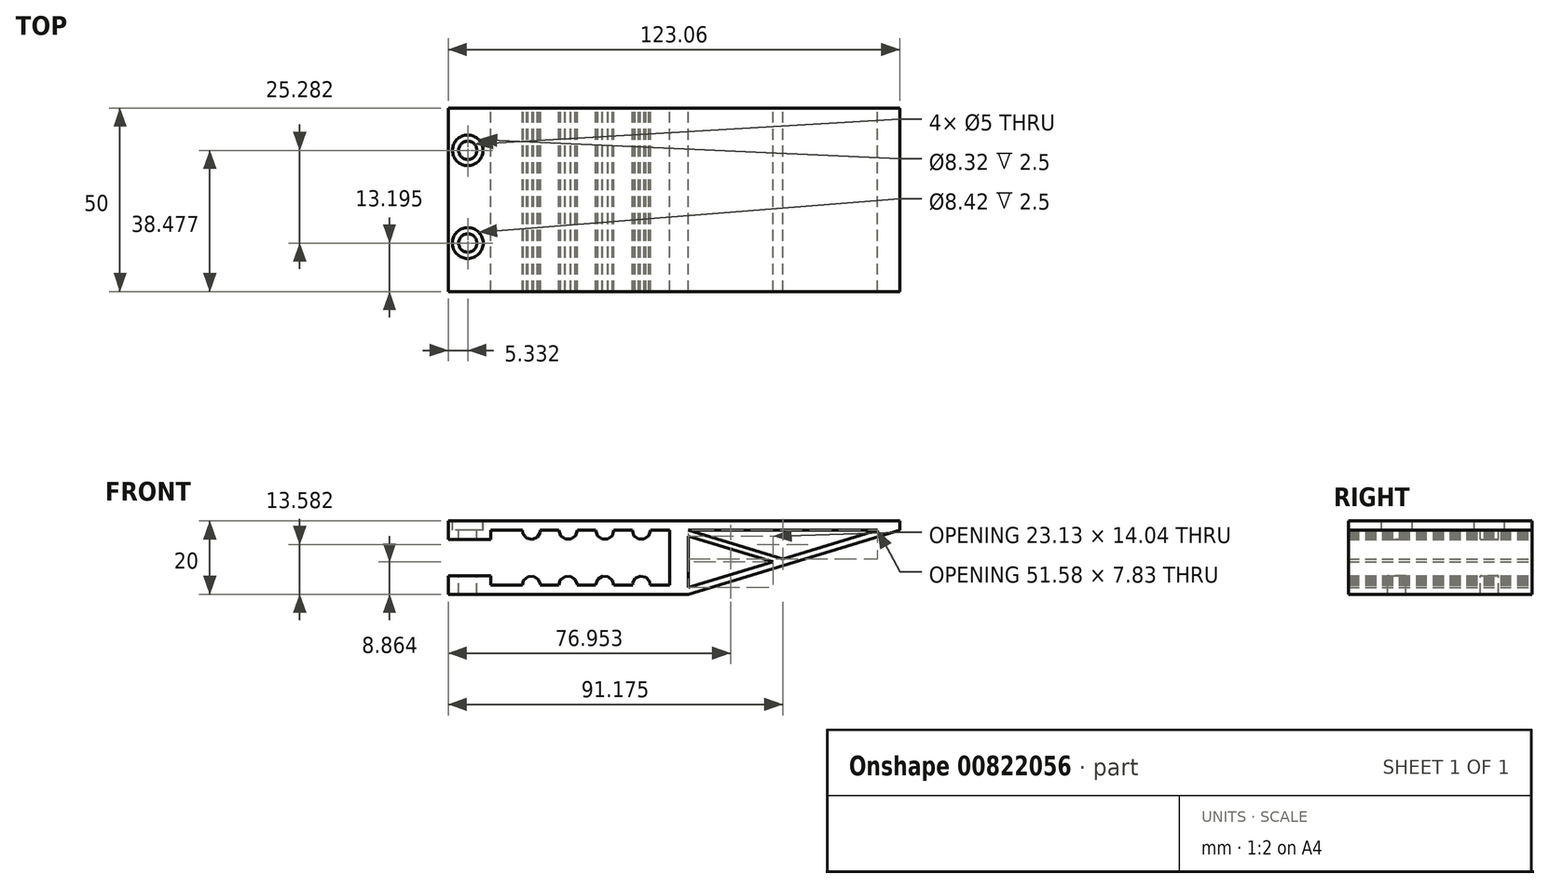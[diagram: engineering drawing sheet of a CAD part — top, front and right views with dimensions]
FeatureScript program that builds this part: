
annotation { "Feature Type Name" : "Feature", "Feature Type Description" : "" }
export const myFeature = defineFeature(function(context is Context, id is Id, definition is map)
    precondition{}
    {
        {
            var Q0;
            Q0=qCreatedBy(makeId("Front.planeOp"),FACE);
            var sketch = newSketch(context, id + "F0", { "sketchPlane" : qUnion([Q0])});
            skLineSegment(sketch, "E0.bottom", {"start": v(-74.58, 29.93) * mm, "end": v(-63, 29.93) * mm});
            skLineSegment(sketch, "E0.top", {"start": v(-74.58, 24.93) * mm, "end": v(-63, 24.93) * mm});
            skLineSegment(sketch, "E0.left", {"start": v(-74.58, 29.93) * mm, "end": v(-74.58, 24.93) * mm});
            skLineSegment(sketch, "E0.right", {"start": v(-63, 29.93) * mm, "end": v(-63, 24.93) * mm});
            skLineSegment(sketch, "E1.bottom", {"start": v(-74.58, 14.93) * mm, "end": v(-63, 14.93) * mm});
            skLineSegment(sketch, "E1.top", {"start": v(-74.58, 9.93) * mm, "end": v(-63, 9.93) * mm});
            skLineSegment(sketch, "E1.left", {"start": v(-74.58, 14.93) * mm, "end": v(-74.58, 9.93) * mm});
            skLineSegment(sketch, "E1.right", {"start": v(-63, 14.93) * mm, "end": v(-63, 9.93) * mm});
            skPoint(sketch, "E2.oppositeSnap0", {"position": v(-63, 27.43) * mm});
            skLineSegment(sketch, "E2.bottom", {"start": v(-63, 29.93) * mm, "end": v(-14.2, 29.93) * mm});
            skLineSegment(sketch, "E2.top", {"start": v(-63, 27.43) * mm, "end": v(-14.2, 27.43) * mm});
            skLineSegment(sketch, "E2.left", {"start": v(-63, 29.93) * mm, "end": v(-63, 27.43) * mm});
            skLineSegment(sketch, "E2.right", {"start": v(-14.2, 29.93) * mm, "end": v(-14.2, 27.43) * mm});
            skLineSegment(sketch, "E3.bottom", {"start": v(-63, 9.93) * mm, "end": v(-14.2, 9.93) * mm});
            skLineSegment(sketch, "E3.top", {"start": v(-63, 12.43) * mm, "end": v(-14.2, 12.43) * mm});
            skLineSegment(sketch, "E3.left", {"start": v(-63, 9.93) * mm, "end": v(-63, 12.43) * mm});
            skLineSegment(sketch, "E3.right", {"start": v(-14.2, 9.93) * mm, "end": v(-14.2, 12.43) * mm});
            skLineSegment(sketch, "E4.bottom", {"start": v(-14.2, 29.93) * mm, "end": v(-9.2, 29.93) * mm});
            skLineSegment(sketch, "E4.top", {"start": v(-14.2, 9.93) * mm, "end": v(-9.2, 9.93) * mm});
            skLineSegment(sketch, "E4.left", {"start": v(-14.2, 29.93) * mm, "end": v(-14.2, 9.93) * mm});
            skLineSegment(sketch, "E4.right", {"start": v(-9.2, 29.93) * mm, "end": v(-9.2, 9.93) * mm});
            skCircle(sketch, "E5.cCircle", {"center": v(-51.92, 27.43) * mm, "radius": 2.5 * mm, "construction": true});
            skLineSegment(sketch, "E5.0", {"start": v(-53.23, 25.3) * mm, "end": v(-54.23, 26.47) * mm});
            skLineSegment(sketch, "E5.1", {"start": v(-54.23, 26.47) * mm, "end": v(-54.35, 28.01) * mm});
            skLineSegment(sketch, "E5.2", {"start": v(-54.35, 28.01) * mm, "end": v(-53.54, 29.33) * mm});
            skLineSegment(sketch, "E5.3", {"start": v(-53.54, 29.33) * mm, "end": v(-52.11, 29.92) * mm});
            skLineSegment(sketch, "E5.4", {"start": v(-52.11, 29.92) * mm, "end": v(-50.61, 29.55) * mm});
            skLineSegment(sketch, "E5.5", {"start": v(-50.61, 29.55) * mm, "end": v(-49.6, 28.38) * mm});
            skLineSegment(sketch, "E5.6", {"start": v(-49.6, 28.38) * mm, "end": v(-49.5, 26.84) * mm});
            skLineSegment(sketch, "E5.7", {"start": v(-49.5, 26.84) * mm, "end": v(-50.3, 25.52) * mm});
            skLineSegment(sketch, "E5.8", {"start": v(-50.3, 25.52) * mm, "end": v(-51.73, 24.93) * mm});
            skLineSegment(sketch, "E5.9", {"start": v(-51.73, 24.93) * mm, "end": v(-53.23, 25.3) * mm});
            skCircle(sketch, "E6.cCircle", {"center": v(-41.92, 27.43) * mm, "radius": 2.5 * mm, "construction": true});
            skLineSegment(sketch, "E6.0", {"start": v(-44.42, 27.43) * mm, "end": v(-43.94, 28.9) * mm});
            skLineSegment(sketch, "E6.1", {"start": v(-43.94, 28.9) * mm, "end": v(-42.7, 29.8) * mm});
            skLineSegment(sketch, "E6.2", {"start": v(-42.7, 29.8) * mm, "end": v(-41.15, 29.8) * mm});
            skLineSegment(sketch, "E6.3", {"start": v(-41.15, 29.8) * mm, "end": v(-39.9, 28.9) * mm});
            skLineSegment(sketch, "E6.4", {"start": v(-39.9, 28.9) * mm, "end": v(-39.42, 27.43) * mm});
            skLineSegment(sketch, "E6.5", {"start": v(-39.42, 27.43) * mm, "end": v(-39.9, 25.96) * mm});
            skLineSegment(sketch, "E6.6", {"start": v(-39.9, 25.96) * mm, "end": v(-41.15, 25.05) * mm});
            skLineSegment(sketch, "E6.7", {"start": v(-41.15, 25.05) * mm, "end": v(-42.7, 25.05) * mm});
            skLineSegment(sketch, "E6.8", {"start": v(-42.7, 25.05) * mm, "end": v(-43.94, 25.96) * mm});
            skLineSegment(sketch, "E6.9", {"start": v(-43.94, 25.96) * mm, "end": v(-44.42, 27.43) * mm});
            skCircle(sketch, "E7.cCircle", {"center": v(-31.92, 27.43) * mm, "radius": 2.5 * mm, "construction": true});
            skLineSegment(sketch, "E7.0", {"start": v(-34.42, 27.43) * mm, "end": v(-33.94, 28.9) * mm});
            skLineSegment(sketch, "E7.1", {"start": v(-33.94, 28.9) * mm, "end": v(-32.7, 29.8) * mm});
            skLineSegment(sketch, "E7.2", {"start": v(-32.7, 29.8) * mm, "end": v(-31.15, 29.8) * mm});
            skLineSegment(sketch, "E7.3", {"start": v(-31.15, 29.8) * mm, "end": v(-29.9, 28.9) * mm});
            skLineSegment(sketch, "E7.4", {"start": v(-29.9, 28.9) * mm, "end": v(-29.42, 27.43) * mm});
            skLineSegment(sketch, "E7.5", {"start": v(-29.42, 27.43) * mm, "end": v(-29.9, 25.96) * mm});
            skLineSegment(sketch, "E7.6", {"start": v(-29.9, 25.96) * mm, "end": v(-31.15, 25.05) * mm});
            skLineSegment(sketch, "E7.7", {"start": v(-31.15, 25.05) * mm, "end": v(-32.7, 25.05) * mm});
            skLineSegment(sketch, "E7.8", {"start": v(-32.7, 25.05) * mm, "end": v(-33.94, 25.96) * mm});
            skLineSegment(sketch, "E7.9", {"start": v(-33.94, 25.96) * mm, "end": v(-34.42, 27.43) * mm});
            skCircle(sketch, "E8.cCircle", {"center": v(-21.92, 27.43) * mm, "radius": 2.5 * mm, "construction": true});
            skLineSegment(sketch, "E8.0", {"start": v(-24.42, 27.43) * mm, "end": v(-23.94, 28.9) * mm});
            skLineSegment(sketch, "E8.1", {"start": v(-23.94, 28.9) * mm, "end": v(-22.7, 29.8) * mm});
            skLineSegment(sketch, "E8.2", {"start": v(-22.7, 29.8) * mm, "end": v(-21.15, 29.8) * mm});
            skLineSegment(sketch, "E8.3", {"start": v(-21.15, 29.8) * mm, "end": v(-19.9, 28.9) * mm});
            skLineSegment(sketch, "E8.4", {"start": v(-19.9, 28.9) * mm, "end": v(-19.42, 27.43) * mm});
            skLineSegment(sketch, "E8.5", {"start": v(-19.42, 27.43) * mm, "end": v(-19.9, 25.96) * mm});
            skLineSegment(sketch, "E8.6", {"start": v(-19.9, 25.96) * mm, "end": v(-21.15, 25.05) * mm});
            skLineSegment(sketch, "E8.7", {"start": v(-21.15, 25.05) * mm, "end": v(-22.7, 25.05) * mm});
            skLineSegment(sketch, "E8.8", {"start": v(-22.7, 25.05) * mm, "end": v(-23.94, 25.96) * mm});
            skLineSegment(sketch, "E8.9", {"start": v(-23.94, 25.96) * mm, "end": v(-24.42, 27.43) * mm});
            skCircle(sketch, "E9.cCircle", {"center": v(-51.92, 12.43) * mm, "radius": 2.5 * mm, "construction": true});
            skLineSegment(sketch, "E9.0", {"start": v(-51.3, 14.85) * mm, "end": v(-50, 14.03) * mm});
            skLineSegment(sketch, "E9.1", {"start": v(-50, 14.03) * mm, "end": v(-49.43, 12.6) * mm});
            skLineSegment(sketch, "E9.2", {"start": v(-49.43, 12.6) * mm, "end": v(-49.8, 11.1) * mm});
            skLineSegment(sketch, "E9.3", {"start": v(-49.8, 11.1) * mm, "end": v(-51, 10.1) * mm});
            skLineSegment(sketch, "E9.4", {"start": v(-51, 10.1) * mm, "end": v(-52.53, 10) * mm});
            skLineSegment(sketch, "E9.5", {"start": v(-52.53, 10) * mm, "end": v(-53.84, 10.82) * mm});
            skLineSegment(sketch, "E9.6", {"start": v(-53.84, 10.82) * mm, "end": v(-54.42, 12.26) * mm});
            skLineSegment(sketch, "E9.7", {"start": v(-54.42, 12.26) * mm, "end": v(-54.04, 13.76) * mm});
            skLineSegment(sketch, "E9.8", {"start": v(-54.04, 13.76) * mm, "end": v(-52.85, 14.75) * mm});
            skLineSegment(sketch, "E9.9", {"start": v(-52.85, 14.75) * mm, "end": v(-51.3, 14.85) * mm});
            skCircle(sketch, "E10.cCircle", {"center": v(-41.92, 12.43) * mm, "radius": 2.5 * mm, "construction": true});
            skLineSegment(sketch, "E10.0", {"start": v(-41.27, 14.84) * mm, "end": v(-39.98, 14) * mm});
            skLineSegment(sketch, "E10.1", {"start": v(-39.98, 14) * mm, "end": v(-39.42, 12.55) * mm});
            skLineSegment(sketch, "E10.2", {"start": v(-39.42, 12.55) * mm, "end": v(-39.83, 11.06) * mm});
            skLineSegment(sketch, "E10.3", {"start": v(-39.83, 11.06) * mm, "end": v(-41.03, 10.09) * mm});
            skLineSegment(sketch, "E10.4", {"start": v(-41.03, 10.09) * mm, "end": v(-42.57, 10.01) * mm});
            skLineSegment(sketch, "E10.5", {"start": v(-42.57, 10.01) * mm, "end": v(-43.87, 10.86) * mm});
            skLineSegment(sketch, "E10.6", {"start": v(-43.87, 10.86) * mm, "end": v(-44.42, 12.3) * mm});
            skLineSegment(sketch, "E10.7", {"start": v(-44.42, 12.3) * mm, "end": v(-44.02, 13.8) * mm});
            skLineSegment(sketch, "E10.8", {"start": v(-44.02, 13.8) * mm, "end": v(-42.81, 14.76) * mm});
            skLineSegment(sketch, "E10.9", {"start": v(-42.81, 14.76) * mm, "end": v(-41.27, 14.84) * mm});
            skCircle(sketch, "E11.cCircle", {"center": v(-31.92, 12.43) * mm, "radius": 2.5 * mm, "construction": true});
            skLineSegment(sketch, "E11.0", {"start": v(-30.98, 14.74) * mm, "end": v(-29.8, 13.75) * mm});
            skLineSegment(sketch, "E11.1", {"start": v(-29.8, 13.75) * mm, "end": v(-29.43, 12.25) * mm});
            skLineSegment(sketch, "E11.2", {"start": v(-29.43, 12.25) * mm, "end": v(-30, 10.82) * mm});
            skLineSegment(sketch, "E11.3", {"start": v(-30, 10.82) * mm, "end": v(-31.32, 10) * mm});
            skLineSegment(sketch, "E11.4", {"start": v(-31.32, 10) * mm, "end": v(-32.86, 10.1) * mm});
            skLineSegment(sketch, "E11.5", {"start": v(-32.86, 10.1) * mm, "end": v(-34.04, 11.1) * mm});
            skLineSegment(sketch, "E11.6", {"start": v(-34.04, 11.1) * mm, "end": v(-34.41, 12.6) * mm});
            skLineSegment(sketch, "E11.7", {"start": v(-34.41, 12.6) * mm, "end": v(-33.84, 14.03) * mm});
            skLineSegment(sketch, "E11.8", {"start": v(-33.84, 14.03) * mm, "end": v(-32.52, 14.85) * mm});
            skLineSegment(sketch, "E11.9", {"start": v(-32.52, 14.85) * mm, "end": v(-30.98, 14.74) * mm});
            skCircle(sketch, "E12.cCircle", {"center": v(-21.92, 12.43) * mm, "radius": 2.5 * mm, "construction": true});
            skLineSegment(sketch, "E12.0", {"start": v(-22.18, 14.91) * mm, "end": v(-20.67, 14.59) * mm});
            skLineSegment(sketch, "E12.1", {"start": v(-20.67, 14.59) * mm, "end": v(-19.64, 13.44) * mm});
            skLineSegment(sketch, "E12.2", {"start": v(-19.64, 13.44) * mm, "end": v(-19.48, 11.9) * mm});
            skLineSegment(sketch, "E12.3", {"start": v(-19.48, 11.9) * mm, "end": v(-20.25, 10.57) * mm});
            skLineSegment(sketch, "E12.4", {"start": v(-20.25, 10.57) * mm, "end": v(-21.66, 9.94) * mm});
            skLineSegment(sketch, "E12.5", {"start": v(-21.66, 9.94) * mm, "end": v(-23.17, 10.26) * mm});
            skLineSegment(sketch, "E12.6", {"start": v(-23.17, 10.26) * mm, "end": v(-24.2, 11.41) * mm});
            skLineSegment(sketch, "E12.7", {"start": v(-24.2, 11.41) * mm, "end": v(-24.37, 12.95) * mm});
            skLineSegment(sketch, "E12.8", {"start": v(-24.37, 12.95) * mm, "end": v(-23.6, 14.29) * mm});
            skLineSegment(sketch, "E12.9", {"start": v(-23.6, 14.29) * mm, "end": v(-22.18, 14.91) * mm});
            skLineSegment(sketch, "E13.bottom", {"start": v(-9.2, 27.43) * mm, "end": v(48.48, 27.43) * mm});
            skLineSegment(sketch, "E13.top", {"start": v(-9.2, 29.93) * mm, "end": v(48.48, 29.93) * mm});
            skLineSegment(sketch, "E13.left", {"start": v(-9.2, 27.43) * mm, "end": v(-9.2, 29.93) * mm});
            skLineSegment(sketch, "E13.right", {"start": v(48.48, 27.43) * mm, "end": v(48.48, 29.93) * mm});
            skLineSegment(sketch, "E14", {"start": v(-9.2, 9.93) * mm, "end": v(48.48, 27.43) * mm});
            skLineSegment(sketch, "E15", {"start": v(42.38, 27.43) * mm, "end": v(-9.2, 11.77) * mm});
            skLineSegment(sketch, "E16", {"start": v(-9.2, 27.43) * mm, "end": v(16.6, 19.6) * mm});
            skLineSegment(sketch, "E17", {"start": v(13.94, 18.8) * mm, "end": v(-9.2, 25.81) * mm});
            skSolve(sketch);
        }
        {
            var Q0;
            Q0=makeQuery(id+"F0.imprint","IMPRINT",FACE,{"disambiguationData":[TD([[makeQuery(id+"F0.imprint","IMPRINT",EDGE,{"derivedFrom":sQuery(id+"F0.wireOp",EDGE,"E1.bottom")}),-1.0]])]});
            var Q1;
            Q1=makeQuery(id+"F0.imprint","IMPRINT",FACE,{"disambiguationData":[TD([[makeQuery(id+"F0.imprint","IMPRINT",EDGE,{"derivedFrom":sQuery(id+"F0.wireOp",EDGE,"E0.bottom")}),-1.0]])]});
            var Q2;
            {var subQ5=sQuery(id+"F0.wireOp",EDGE,"E5.0");Q2=makeQuery(id+"F0.imprint","IMPRINT",FACE,{"disambiguationData":[TD([[makeQuery(id+"F0.imprint","IMPRINT",EDGE,{"derivedFrom":subQ5}),-1.0]])]});}
            var Q3;
            {var subQ9=sQuery(id+"F0.wireOp",EDGE,"E2.bottom");Q3=makeQuery(id+"F0.imprint","IMPRINT",FACE,{"disambiguationData":[TD([[makeQuery(id+"F0.imprint","IMPRINT",EDGE,{"derivedFrom":subQ9}),-1.0]])]});}
            var Q4;
            {var subQ0=sQuery(id+"F0.wireOp",EDGE,"E5.2");Q4=makeQuery(id+"F0.imprint","IMPRINT",FACE,{"disambiguationData":[TD([[makeQuery(id+"F0.imprint","IMPRINT",EDGE,{"derivedFrom":subQ0}),-1.0]])]});}
            var Q5;
            {var subQ0=sQuery(id+"F0.wireOp",EDGE,"E6.0");Q5=makeQuery(id+"F0.imprint","IMPRINT",FACE,{"disambiguationData":[TD([[makeQuery(id+"F0.imprint","IMPRINT",EDGE,{"derivedFrom":subQ0}),-1.0]])]});}
            var Q6;
            {var subQ2=sQuery(id+"F0.wireOp",EDGE,"E6.5");Q6=makeQuery(id+"F0.imprint","IMPRINT",FACE,{"disambiguationData":[TD([[makeQuery(id+"F0.imprint","IMPRINT",EDGE,{"derivedFrom":subQ2}),-1.0]])]});}
            var Q7;
            {var subQ0=sQuery(id+"F0.wireOp",EDGE,"E7.5");Q7=makeQuery(id+"F0.imprint","IMPRINT",FACE,{"disambiguationData":[TD([[makeQuery(id+"F0.imprint","IMPRINT",EDGE,{"derivedFrom":subQ0}),-1.0]])]});}
            var Q8;
            {var subQ0=sQuery(id+"F0.wireOp",EDGE,"E7.0");Q8=makeQuery(id+"F0.imprint","IMPRINT",FACE,{"disambiguationData":[TD([[makeQuery(id+"F0.imprint","IMPRINT",EDGE,{"derivedFrom":subQ0}),-1.0]])]});}
            var Q9;
            {var subQ0=sQuery(id+"F0.wireOp",EDGE,"E8.0");Q9=makeQuery(id+"F0.imprint","IMPRINT",FACE,{"disambiguationData":[TD([[makeQuery(id+"F0.imprint","IMPRINT",EDGE,{"derivedFrom":subQ0}),-1.0]])]});}
            var Q10;
            {var subQ0=sQuery(id+"F0.wireOp",EDGE,"E8.5");Q10=makeQuery(id+"F0.imprint","IMPRINT",FACE,{"disambiguationData":[TD([[makeQuery(id+"F0.imprint","IMPRINT",EDGE,{"derivedFrom":subQ0}),-1.0]])]});}
            var Q11;
            Q11=makeQuery(id+"F0.imprint","IMPRINT",FACE,{"disambiguationData":[TD([[makeQuery(id+"F0.imprint","IMPRINT",EDGE,{"derivedFrom":sQuery(id+"F0.wireOp",EDGE,"E9.0")}),-1.0]])]});
            var Q12;
            {var subQ0=sQuery(id+"F0.wireOp",EDGE,"E9.3");Q12=makeQuery(id+"F0.imprint","IMPRINT",FACE,{"disambiguationData":[TD([[makeQuery(id+"F0.imprint","IMPRINT",EDGE,{"derivedFrom":subQ0}),-1.0]])]});}
            var Q13;
            Q13=makeQuery(id+"F0.imprint","IMPRINT",FACE,{"disambiguationData":[TD([[makeQuery(id+"F0.imprint","IMPRINT",EDGE,{"derivedFrom":sQuery(id+"F0.wireOp",EDGE,"E10.0")}),-1.0]])]});
            var Q14;
            {var subQ0=sQuery(id+"F0.wireOp",EDGE,"E10.3");Q14=makeQuery(id+"F0.imprint","IMPRINT",FACE,{"disambiguationData":[TD([[makeQuery(id+"F0.imprint","IMPRINT",EDGE,{"derivedFrom":subQ0}),-1.0]])]});}
            var Q15;
            {var subQ4=sQuery(id+"F0.wireOp",EDGE,"E11.0");Q15=makeQuery(id+"F0.imprint","IMPRINT",FACE,{"disambiguationData":[TD([[makeQuery(id+"F0.imprint","IMPRINT",EDGE,{"derivedFrom":subQ4}),-1.0]])]});}
            var Q16;
            {var subQ0=sQuery(id+"F0.wireOp",EDGE,"E11.2");Q16=makeQuery(id+"F0.imprint","IMPRINT",FACE,{"disambiguationData":[TD([[makeQuery(id+"F0.imprint","IMPRINT",EDGE,{"derivedFrom":subQ0}),-1.0]])]});}
            var Q17;
            Q17=makeQuery(id+"F0.imprint","IMPRINT",FACE,{"disambiguationData":[TD([[makeQuery(id+"F0.imprint","IMPRINT",EDGE,{"derivedFrom":sQuery(id+"F0.wireOp",EDGE,"E12.0")}),-1.0]])]});
            var Q18;
            {var subQ0=sQuery(id+"F0.wireOp",EDGE,"E12.3");Q18=makeQuery(id+"F0.imprint","IMPRINT",FACE,{"disambiguationData":[TD([[makeQuery(id+"F0.imprint","IMPRINT",EDGE,{"derivedFrom":subQ0}),-1.0]])]});}
            var Q19;
            {var subQ15=sQuery(id+"F0.wireOp",EDGE,"E3.bottom");Q19=makeQuery(id+"F0.imprint","IMPRINT",FACE,{"disambiguationData":[TD([[makeQuery(id+"F0.imprint","IMPRINT",EDGE,{"derivedFrom":subQ15}),1.0]])]});}
            var Q20;
            {var subQ3=sQuery(id+"F0.wireOp",EDGE,"E4.bottom");Q20=makeQuery(id+"F0.imprint","IMPRINT",FACE,{"disambiguationData":[TD([[makeQuery(id+"F0.imprint","IMPRINT",EDGE,{"derivedFrom":subQ3}),-1.0]])]});}
            var Q21;
            Q21=makeQuery(id+"F0.imprint","IMPRINT",FACE,{"disambiguationData":[TD([[makeQuery(id+"F0.imprint","IMPRINT",EDGE,{"derivedFrom":sQuery(id+"F0.wireOp",EDGE,"E13.top")}),-1.0]])]});
            var Q22;
            {var subQ0=sQuery(id+"F0.wireOp",EDGE,"E16");Q22=makeQuery(id+"F0.imprint","IMPRINT",FACE,{"disambiguationData":[TD([[makeQuery(id+"F0.imprint","IMPRINT",EDGE,{"derivedFrom":subQ0}),-1.0]])]});}
            var Q23;
            {var subQ0=sQuery(id+"F0.wireOp",EDGE,"E14");Q23=makeQuery(id+"F0.imprint","IMPRINT",FACE,{"disambiguationData":[TD([[makeQuery(id+"F0.imprint","IMPRINT",EDGE,{"derivedFrom":subQ0}),1.0]])]});}
            extrude(context, id + "F1", {"entities" : qUnion([Q0, Q1, Q2, Q3, Q4, Q5, Q6, Q7, Q8, Q9, Q10, Q11, Q12, Q13, Q14, Q15, Q16, Q17, Q18, Q19, Q20, Q21, Q22, Q23]), "depth" : 50 * mm, "offsetDistance" : 25 * mm});
        }
        {
            var Q0;
            Q0=makeQuery(id+"F1.opExtrude","SWEPT_FACE",FACE,{"disambiguationData":[OSD([sQuery(id+"F0.wireOp",EDGE,"E0.bottom"),sQuery(id+"F0.wireOp",EDGE,"E2.bottom"),sQuery(id+"F0.wireOp",EDGE,"E4.bottom"),sQuery(id+"F0.wireOp",EDGE,"E13.top")])]});
            var sketch = newSketch(context, id + "F2", { "sketchPlane" : qUnion([Q0])});
            skPoint(sketch, "E18", {"position": v(-69.25, -11.52) * mm});
            skPoint(sketch, "E19", {"position": v(-69.25, -36.8) * mm});
            skSolve(sketch);
        }
        {
            var Q0;
            Q0=sQuery(id+"F2.wireOp",VERTEX,"E18");
            var Q1;
            Q1=sQuery(id+"F2.wireOp",VERTEX,"E19");
            var Q2;
            Q2=makeQuery(id+"F1.opExtrude","SWEPT_BODY",BODY,{"disambiguationData":[OSD([sQuery(id+"F0.wireOp",EDGE,"E0.bottom"),sQuery(id+"F0.wireOp",EDGE,"E0.top"),sQuery(id+"F0.wireOp",EDGE,"E0.left"),sQuery(id+"F0.wireOp",EDGE,"E0.right"),sQuery(id+"F0.wireOp",EDGE,"E1.bottom"),sQuery(id+"F0.wireOp",EDGE,"E1.top"),sQuery(id+"F0.wireOp",EDGE,"E1.left"),sQuery(id+"F0.wireOp",EDGE,"E1.right"),sQuery(id+"F0.wireOp",EDGE,"E2.bottom"),sQuery(id+"F0.wireOp",EDGE,"E2.top"),sQuery(id+"F0.wireOp",EDGE,"E3.bottom"),sQuery(id+"F0.wireOp",EDGE,"E3.top"),sQuery(id+"F0.wireOp",EDGE,"E4.bottom"),sQuery(id+"F0.wireOp",EDGE,"E4.top"),sQuery(id+"F0.wireOp",EDGE,"E4.left"),sQuery(id+"F0.wireOp",EDGE,"E4.right"),sQuery(id+"F0.wireOp",EDGE,"E5.0"),sQuery(id+"F0.wireOp",EDGE,"E5.1"),sQuery(id+"F0.wireOp",EDGE,"E5.6"),sQuery(id+"F0.wireOp",EDGE,"E5.7"),sQuery(id+"F0.wireOp",EDGE,"E5.8"),sQuery(id+"F0.wireOp",EDGE,"E5.9"),sQuery(id+"F0.wireOp",EDGE,"E6.5"),sQuery(id+"F0.wireOp",EDGE,"E6.6"),sQuery(id+"F0.wireOp",EDGE,"E6.7"),sQuery(id+"F0.wireOp",EDGE,"E6.8"),sQuery(id+"F0.wireOp",EDGE,"E6.9"),sQuery(id+"F0.wireOp",EDGE,"E7.5"),sQuery(id+"F0.wireOp",EDGE,"E7.6"),sQuery(id+"F0.wireOp",EDGE,"E7.7"),sQuery(id+"F0.wireOp",EDGE,"E7.8"),sQuery(id+"F0.wireOp",EDGE,"E7.9"),sQuery(id+"F0.wireOp",EDGE,"E8.5"),sQuery(id+"F0.wireOp",EDGE,"E8.6"),sQuery(id+"F0.wireOp",EDGE,"E8.7"),sQuery(id+"F0.wireOp",EDGE,"E8.8"),sQuery(id+"F0.wireOp",EDGE,"E8.9"),sQuery(id+"F0.wireOp",EDGE,"E9.0"),sQuery(id+"F0.wireOp",EDGE,"E9.1"),sQuery(id+"F0.wireOp",EDGE,"E9.2"),sQuery(id+"F0.wireOp",EDGE,"E9.7"),sQuery(id+"F0.wireOp",EDGE,"E9.8"),sQuery(id+"F0.wireOp",EDGE,"E9.9"),sQuery(id+"F0.wireOp",EDGE,"E10.0"),sQuery(id+"F0.wireOp",EDGE,"E10.1"),sQuery(id+"F0.wireOp",EDGE,"E10.2"),sQuery(id+"F0.wireOp",EDGE,"E10.7"),sQuery(id+"F0.wireOp",EDGE,"E10.8"),sQuery(id+"F0.wireOp",EDGE,"E10.9"),sQuery(id+"F0.wireOp",EDGE,"E11.0"),sQuery(id+"F0.wireOp",EDGE,"E11.1"),sQuery(id+"F0.wireOp",EDGE,"E11.6"),sQuery(id+"F0.wireOp",EDGE,"E11.7"),sQuery(id+"F0.wireOp",EDGE,"E11.8"),sQuery(id+"F0.wireOp",EDGE,"E11.9"),sQuery(id+"F0.wireOp",EDGE,"E12.0"),sQuery(id+"F0.wireOp",EDGE,"E12.1"),sQuery(id+"F0.wireOp",EDGE,"E12.2"),sQuery(id+"F0.wireOp",EDGE,"E12.7"),sQuery(id+"F0.wireOp",EDGE,"E12.8"),sQuery(id+"F0.wireOp",EDGE,"E12.9"),sQuery(id+"F0.wireOp",EDGE,"E13.bottom"),sQuery(id+"F0.wireOp",EDGE,"E13.top"),sQuery(id+"F0.wireOp",EDGE,"E13.right"),sQuery(id+"F0.wireOp",EDGE,"E14"),sQuery(id+"F0.wireOp",EDGE,"E15"),sQuery(id+"F0.wireOp",EDGE,"E16"),sQuery(id+"F0.wireOp",EDGE,"E17")])]});
            hole(context, id + "F3", {"style" : HoleStyle.SIMPLE, "endStyle" : HoleEndStyle.BLIND, "holeDiameter" : 5 * mm, "majorDiameter" : 5 * mm, "holeDepth" : 30 * mm, "isTappedThrough" : true, "tappedDepth" : 12 * mm, "tapClearance" : 3, "locations" : qUnion([Q0, Q1]), "scope" : qUnion([Q2])});
        }
        {
            var Q0;
            Q0=makeQuery(id+"F1.opExtrude","SWEPT_FACE",FACE,{"disambiguationData":[OSD([sQuery(id+"F0.wireOp",EDGE,"E0.bottom"),sQuery(id+"F0.wireOp",EDGE,"E2.bottom"),sQuery(id+"F0.wireOp",EDGE,"E4.bottom"),sQuery(id+"F0.wireOp",EDGE,"E13.top")])]});
            var sketch = newSketch(context, id + "F4", { "sketchPlane" : qUnion([Q0])});
            skCircle(sketch, "E20", {"center": v(-69.25, -36.8) * mm, "radius": 4.21 * mm});
            skCircle(sketch, "E21", {"center": v(-69.25, -11.52) * mm, "radius": 4.16 * mm});
            skSolve(sketch);
        }
        {
            var Q0;
            Q0=makeQuery(id+"F4.imprint","IMPRINT",FACE,{"disambiguationData":[TD([[makeQuery(id+"F4.imprint","IMPRINT",EDGE,{"derivedFrom":sQuery(id+"F4.wireOp",EDGE,"E21")}),1.0]])]});
            var Q1;
            Q1=makeQuery(id+"F4.imprint","IMPRINT",FACE,{"disambiguationData":[TD([[makeQuery(id+"F4.imprint","IMPRINT",EDGE,{"derivedFrom":sQuery(id+"F4.wireOp",EDGE,"E20")}),1.0]])]});
            extrude(context, id + "F5", {"entities" : qUnion([Q0, Q1]), "operationType" : NewBodyOperationType.REMOVE, "oppositeDirection" : true, "depth" : 2.5 * mm, "offsetDistance" : 25 * mm});
        }
    });
